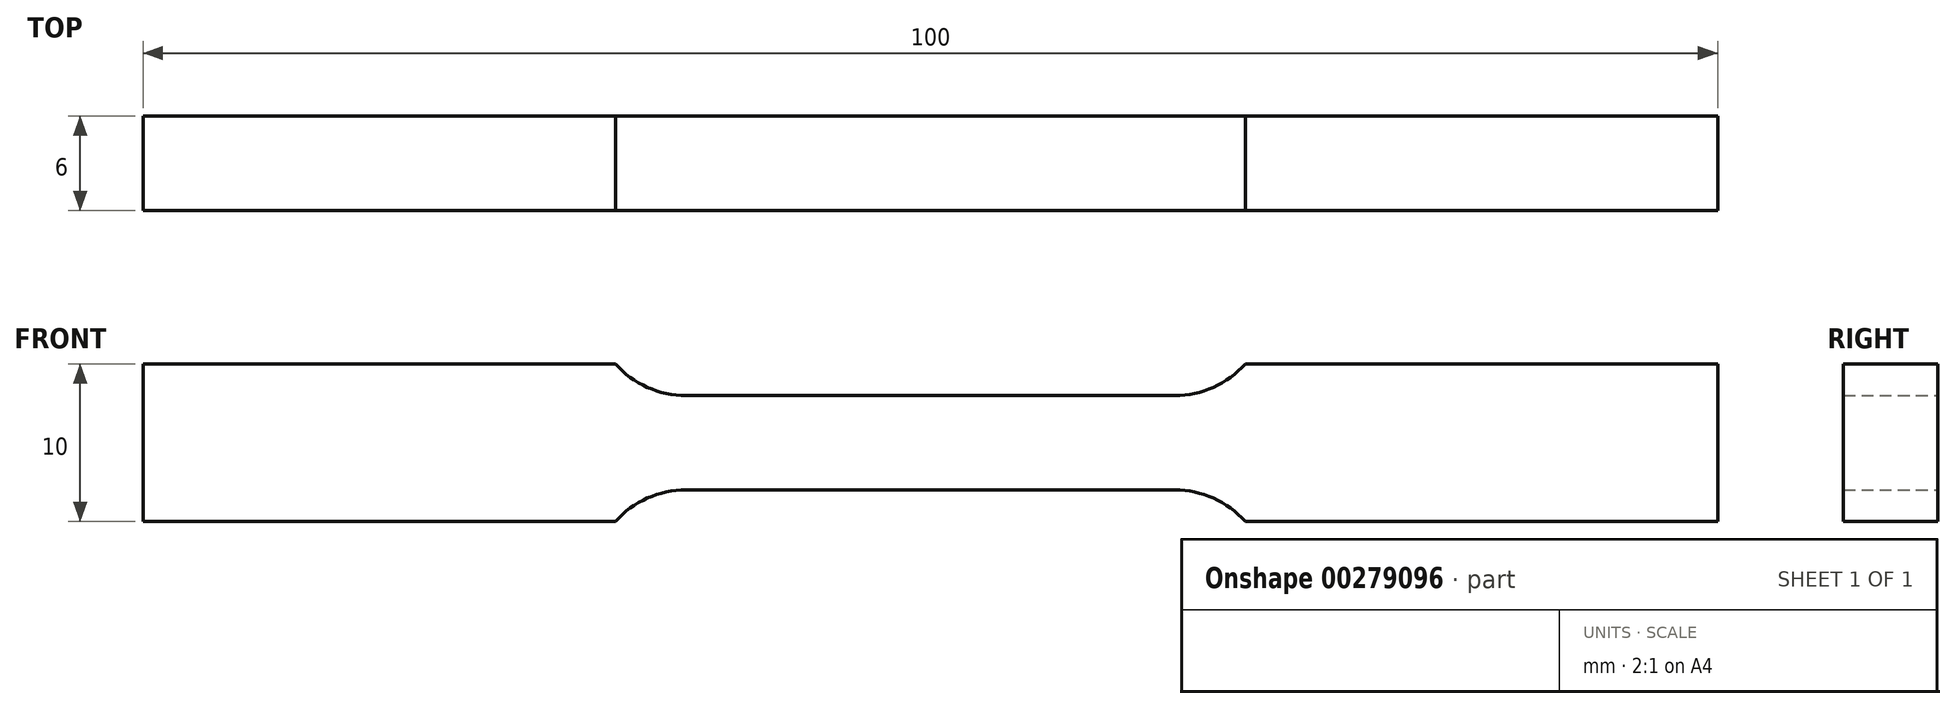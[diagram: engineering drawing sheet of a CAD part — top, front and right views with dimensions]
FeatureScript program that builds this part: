
annotation { "Feature Type Name" : "Feature", "Feature Type Description" : "" }
export const myFeature = defineFeature(function(context is Context, id is Id, definition is map)
    precondition{}
    {
        {
            var Q0;
            Q0=qCreatedBy(makeId("Front.planeOp"),FACE);
            var sketch = newSketch(context, id + "F0", { "sketchPlane" : qUnion([Q0])});
            skLineSegment(sketch, "E0", {"start": v(0, 3) * mm, "end": v(15.53, 3) * mm});
            skArc(sketch, "E1", {"start": v(15.53, 3) * mm, "mid": v(17.98, 3.52) * mm, "end": v(20, 5) * mm});
            skLineSegment(sketch, "E2", {"start": v(20, 5) * mm, "end": v(50, 5) * mm});
            skLineSegment(sketch, "E3", {"start": v(50, 5) * mm, "end": v(50, 0) * mm});
            skLineSegment(sketch, "E4.MirrorCS", {"start": v(0, -3) * mm, "end": v(15.53, -3) * mm});
            skLineSegment(sketch, "E5.MirrorCS", {"start": v(50, -5) * mm, "end": v(50, 0) * mm});
            skLineSegment(sketch, "E6.MirrorCS", {"start": v(20, -5) * mm, "end": v(50, -5) * mm});
            skArc(sketch, "E7.MirrorCS", {"start": v(15.53, -3) * mm, "mid": v(17.98, -3.52) * mm, "end": v(20, -5) * mm});
            skArc(sketch, "E8.MirrorCS", {"start": v(-15.53, -3) * mm, "mid": v(-17.98, -3.52) * mm, "end": v(-20, -5) * mm});
            skLineSegment(sketch, "E9.MirrorCS", {"start": v(-20, -5) * mm, "end": v(-50, -5) * mm});
            skArc(sketch, "E10.MirrorCS", {"start": v(-15.53, 3) * mm, "mid": v(-17.98, 3.52) * mm, "end": v(-20, 5) * mm});
            skLineSegment(sketch, "E11.MirrorCS", {"start": v(-20, 5) * mm, "end": v(-50, 5) * mm});
            skLineSegment(sketch, "E12.MirrorCS", {"start": v(-50, -5) * mm, "end": v(-50, 0) * mm});
            skLineSegment(sketch, "E13.MirrorCS", {"start": v(0, -3) * mm, "end": v(-15.53, -3) * mm});
            skLineSegment(sketch, "E14.MirrorCS", {"start": v(-50, 5) * mm, "end": v(-50, 0) * mm});
            skLineSegment(sketch, "E15.MirrorCS", {"start": v(0, 3) * mm, "end": v(-15.53, 3) * mm});
            skSolve(sketch);
        }
        {
            var Q0;
            Q0=makeQuery(id+"F0.imprint","IMPRINT",FACE,{"disambiguationData":[TD([[makeQuery(id+"F0.imprint","IMPRINT",EDGE,{"derivedFrom":sQuery(id+"F0.wireOp",EDGE,"E0")}),-1.0]])]});
            extrude(context, id + "F1", {"entities" : qUnion([Q0]), "endBound" : BoundingType.SYMMETRIC, "depth" : 6 * mm});
        }
    });
